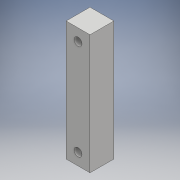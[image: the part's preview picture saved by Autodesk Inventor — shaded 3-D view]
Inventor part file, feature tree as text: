
AUTODESK INVENTOR PART (.ipt)
format: ipt  version: 2018 (Build 220112000, 112)  size: 103,424 bytes
history: native  units: mm
features: sketch x2, extrude x1, hole x1
ambient origin geometry x8: Origin, YZ Plane, XZ Plane, XY Plane, X Axis, Y Axis, Z Axis, Center Point
bodies: Body1 (feature_tree)
feature tree (4):
  extrude  "押し出し2"  Depth=30.0mm
  hole  "穴2"  [1 undecoded]
  sketch  "スケッチ4"
  sketch  "スケッチ5"
note: 1 required parameter value undecoded (feature->parameter linkage not recoverable at this tier; creation-order binding heuristic only, values carry confidence <= 0.55)
